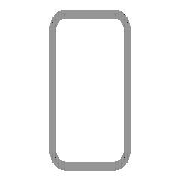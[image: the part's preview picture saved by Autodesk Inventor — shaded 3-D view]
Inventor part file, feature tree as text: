
AUTODESK INVENTOR PART (.ipt)
format: ipt  version: 2025 (Build 290162010, 162A)  size: 133,120 bytes
history: native  units: mm (DEFAULTED — no unit token found)
features: other x4, sketch x1, plane x1
ambient origin geometry x8: Origin, YZ Plane, XZ Plane, XY Plane, X Axis, Y Axis, Z Axis, Center Point
bodies: Solid1 (feature_tree), Body (feature_tree)
feature tree (6):
  parser-record x1  (decoder bookkeeping rows leaked as tree rows — omitted from the tree; the rows remain in map.json)
  other  "Driven Length"
  other  "Start Plane"
  other  "End Plane"
  sketch  "Sketch3"  dims[d3=989.0mm d4=0.0mm d7=6.0mm d9=40.0mm d11=60.0mm d12=3.0mm d13=-0.0mm d14=989.0mm d15=20.0mm d16=30.0mm d17=90.0deg d18=989.0mm]
  plane  "Work Plane3"
